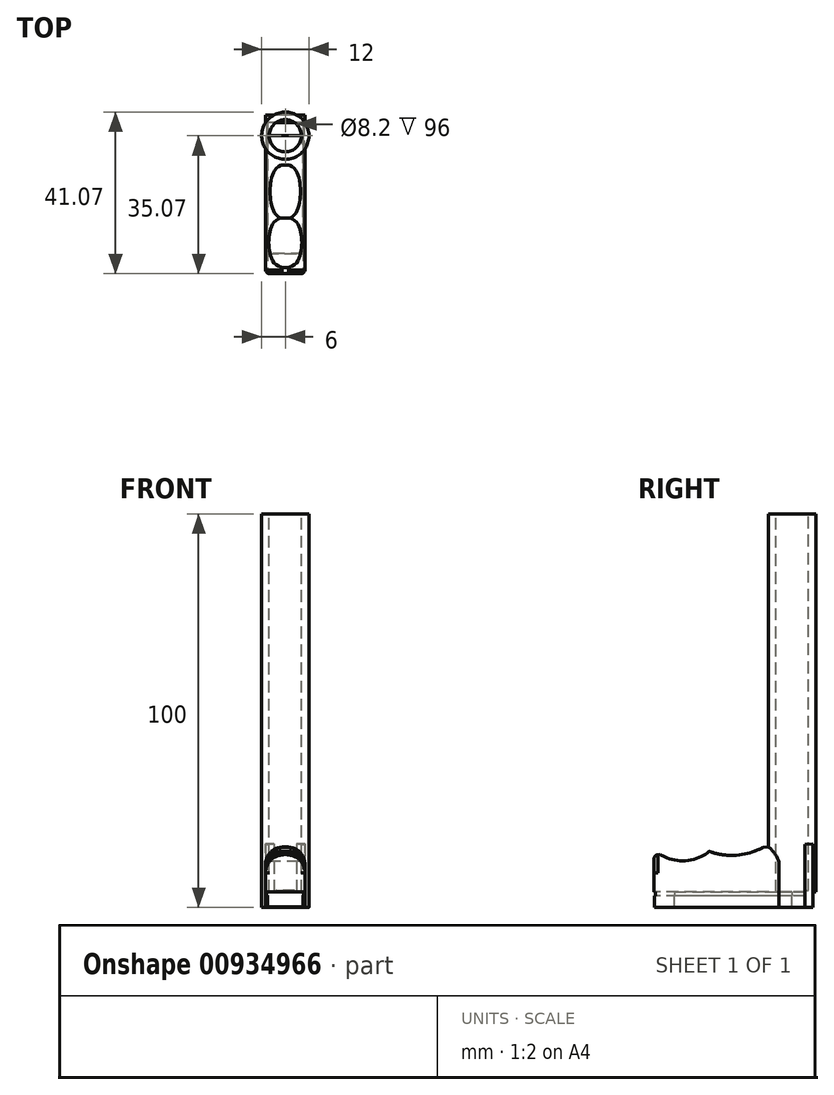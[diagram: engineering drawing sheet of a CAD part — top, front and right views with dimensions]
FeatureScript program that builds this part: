
annotation { "Feature Type Name" : "Feature", "Feature Type Description" : "" }
export const myFeature = defineFeature(function(context is Context, id is Id, definition is map)
    precondition{}
    {
        {
            var Q0;
            Q0=qCreatedBy(makeId("Top.planeOp"),FACE);
            var sketch = newSketch(context, id + "F0", { "sketchPlane" : qUnion([Q0])});
            skCircle(sketch, "E0", {"center": v(0, 0) * mm, "radius": 6 * mm});
            skSolve(sketch);
        }
        {
            var Q0;
            Q0=makeQuery(id+"F0.imprint","IMPRINT",FACE,{"disambiguationData":[TD([[makeQuery(id+"F0.imprint","IMPRINT",EDGE,{"derivedFrom":sQuery(id+"F0.wireOp",EDGE,"E0")}),1.0]])]});
            extrude(context, id + "F1", {"entities" : qUnion([Q0]), "depth" : 100 * mm, "offsetDistance" : 25 * mm});
        }
        {
            var Q0;
            Q0=qCreatedBy(makeId("Right.planeOp"),FACE);
            var sketch = newSketch(context, id + "F2", { "sketchPlane" : qUnion([Q0])});
            skLineSegment(sketch, "E1", {"start": v(-35.07, 0) * mm, "end": v(-35.07, 13.3) * mm});
            skLineSegment(sketch, "E2", {"start": v(-35.07, 0) * mm, "end": v(5.26, 0) * mm});
            skLineSegment(sketch, "E3", {"start": v(5.26, 0) * mm, "end": v(5.26, 16.15) * mm});
            skLineSegment(sketch, "E4", {"start": v(5.26, 16.15) * mm, "end": v(-35.07, 13.3) * mm});
            skSolve(sketch);
        }
        {
            var Q0;
            Q0=makeQuery(id+"F2.imprint","IMPRINT",FACE,{"disambiguationData":[TD([[makeQuery(id+"F2.imprint","IMPRINT",EDGE,{"derivedFrom":sQuery(id+"F2.wireOp",EDGE,"E1")}),-1.0]])]});
            extrude(context, id + "F3", {"entities" : qUnion([Q0]), "operationType" : NewBodyOperationType.ADD, "depth" : 5 * mm, "offsetDistance" : 25 * mm, "hasSecondDirection" : true, "secondDirectionOppositeDirection" : true, "secondDirectionDepth" : 5 * mm});
        }
        {
            var Q0;
            Q0=makeQuery(id+"F1.opExtrude","CAP_FACE",FACE,{"disambiguationData":[OSD([sQuery(id+"F0.wireOp",EDGE,"E0")])],"isStart":false});
            var sketch = newSketch(context, id + "F4", { "sketchPlane" : qUnion([Q0])});
            skCircle(sketch, "E5", {"center": v(0, 0) * mm, "radius": 4.1 * mm});
            skSolve(sketch);
        }
        {
            var Q0;
            Q0=makeQuery(id+"F4.imprint","IMPRINT",FACE,{"disambiguationData":[TD([[makeQuery(id+"F4.imprint","IMPRINT",EDGE,{"derivedFrom":sQuery(id+"F4.wireOp",EDGE,"E5")}),1.0]])]});
            extrude(context, id + "F5", {"entities" : qUnion([Q0]), "operationType" : NewBodyOperationType.REMOVE, "oppositeDirection" : true, "depth" : 125.4 * mm, "offsetDistance" : 25 * mm});
        }
        {
            var Q0;
            Q0=makeQuery(id+"F3.opExtrude","SWEPT_FACE",FACE,{"disambiguationData":[OSD([sQuery(id+"F2.wireOp",EDGE,"E1")])]});
            var sketch = newSketch(context, id + "F6", { "sketchPlane" : qUnion([Q0])});
            skLineSegment(sketch, "E6", {"start": v(-4.5, 0) * mm, "end": v(-4.5, 3) * mm});
            skLineSegment(sketch, "E7", {"start": v(-4.5, 3) * mm, "end": v(-4.74, 3) * mm});
            skLineSegment(sketch, "E8", {"start": v(-4.74, 3) * mm, "end": v(-4.74, 4) * mm});
            skLineSegment(sketch, "E9", {"start": v(-4.74, 4) * mm, "end": v(4.77, 4) * mm});
            skLineSegment(sketch, "E10", {"start": v(4.77, 4) * mm, "end": v(4.77, 3) * mm});
            skLineSegment(sketch, "E11", {"start": v(4.77, 3) * mm, "end": v(4.5, 3) * mm});
            skLineSegment(sketch, "E12", {"start": v(4.5, 3) * mm, "end": v(4.5, 0) * mm});
            skLineSegment(sketch, "E13", {"start": v(4.5, 0) * mm, "end": v(-4.5, 0) * mm});
            skSolve(sketch);
        }
        {
            var Q0;
            Q0 = qSketchRegion(id + "F6", true);
            extrude(context, id + "F7", {"entities" : qUnion([Q0]), "operationType" : NewBodyOperationType.REMOVE, "endBound" : BoundingType.THROUGH_ALL, "oppositeDirection" : true, "depth" : 25 * mm, "offsetDistance" : 25 * mm});
        }
        {
            var Q0;
            Q0=qCreatedBy(makeId("Front.planeOp"),FACE);
            var sketch = newSketch(context, id + "F8", { "sketchPlane" : qUnion([Q0])});
            skLineSegment(sketch, "E14", {"start": v(-4.45, 0.2) * mm, "end": v(-4.45, 3.1) * mm});
            skLineSegment(sketch, "E15", {"start": v(-4.45, 3.1) * mm, "end": v(-4.75, 3.1) * mm});
            skLineSegment(sketch, "E16", {"start": v(-4.75, 3.1) * mm, "end": v(-4.75, 4) * mm});
            skLineSegment(sketch, "E17", {"start": v(-4.75, 4) * mm, "end": v(4.65, 4) * mm});
            skLineSegment(sketch, "E18", {"start": v(4.65, 4) * mm, "end": v(4.65, 3.1) * mm});
            skLineSegment(sketch, "E19", {"start": v(4.65, 3.1) * mm, "end": v(4.45, 3.1) * mm});
            skLineSegment(sketch, "E20", {"start": v(4.45, 3.1) * mm, "end": v(4.45, 0.2) * mm});
            skLineSegment(sketch, "E21", {"start": v(4.45, 0.2) * mm, "end": v(-4.45, 0.2) * mm});
            skSolve(sketch);
        }
        {
            var Q0;
            Q0=makeQuery(id+"F8.imprint","IMPRINT",FACE,{"disambiguationData":[TD([[makeQuery(id+"F8.imprint","IMPRINT",EDGE,{"derivedFrom":sQuery(id+"F8.wireOp",EDGE,"E14")}),-1.0]])]});
            var Q1;
            Q1=sQuery(id+"F8.wireOp",EDGE,"E14");
            var Q2;
            Q2=sQuery(id+"F8.wireOp",EDGE,"E15");
            var Q3;
            Q3=sQuery(id+"F8.wireOp",EDGE,"E16");
            var Q4;
            Q4=sQuery(id+"F8.wireOp",EDGE,"E17");
            var Q5;
            Q5=sQuery(id+"F8.wireOp",EDGE,"E18");
            var Q6;
            Q6=sQuery(id+"F8.wireOp",EDGE,"E19");
            var Q7;
            Q7=sQuery(id+"F8.wireOp",EDGE,"E20");
            var Q8;
            Q8=sQuery(id+"F8.wireOp",EDGE,"E21");
            extrude(context, id + "F9", {"entities" : qUnion([Q0]), "surfaceEntities" : qUnion([Q1, Q2, Q3, Q4, Q5, Q6, Q7, Q8]), "depth" : 29.9 * mm, "offsetDistance" : 25 * mm});
        }
        {
            var Q0;
            {var subQ0=sQuery(id+"F2.wireOp",EDGE,"E3");var subQ1=sQuery(id+"F2.wireOp",EDGE,"E2");var subQ3=sQuery(id+"F2.wireOp",EDGE,"E4");Q0=makeQuery(id+"F3.boolean.opBoolean","SPLIT",FACE,{"disambiguationData":[TD([makeQuery(id+"F3.opExtrude","SWEPT_FACE",FACE,{"disambiguationData":[OSD([subQ0])]})])],"derivedFrom":makeQuery(id+"F3.opExtrude","CAP_FACE",FACE,{"disambiguationData":[OSD([sQuery(id+"F2.wireOp",EDGE,"E1"),subQ1,subQ0,subQ3])],"isStart":true})});}
            var sketch = newSketch(context, id + "F10", { "sketchPlane" : qUnion([Q0])});
            skLineSegment(sketch, "E22.bottom", {"start": v(-5.26, 0) * mm, "end": v(-3.32, 0) * mm});
            skLineSegment(sketch, "E22.top", {"start": v(-5.26, 4.31) * mm, "end": v(-3.32, 4.31) * mm});
            skLineSegment(sketch, "E22.left", {"start": v(-5.26, 0) * mm, "end": v(-5.26, 4.31) * mm});
            skLineSegment(sketch, "E22.right", {"start": v(-3.32, 0) * mm, "end": v(-3.32, 4.31) * mm});
            skSolve(sketch);
        }
        {
            var Q0;
            Q0=makeQuery(id+"F10.imprint","IMPRINT",FACE,{"disambiguationData":[TD([[makeQuery(id+"F10.imprint","IMPRINT",EDGE,{"derivedFrom":sQuery(id+"F10.wireOp",EDGE,"E22.bottom")}),-1.0]])]});
            extrude(context, id + "F11", {"entities" : qUnion([Q0]), "operationType" : NewBodyOperationType.ADD, "oppositeDirection" : true, "depth" : 9.9 * mm, "offsetDistance" : 25 * mm});
        }
        {
            var Q0;
            {var subQ0=sQuery(id+"F2.wireOp",EDGE,"E4");var subQ1=sQuery(id+"F2.wireOp",EDGE,"E1");Q0=makeQuery(id+"F3.boolean.opBoolean","SPLIT",EDGE,{"disambiguationData":[TD([makeQuery(id+"F3.opExtrude","SWEPT_FACE",FACE,{"disambiguationData":[OSD([subQ1])]})])],"derivedFrom":makeQuery(id+"F3.opExtrude","CAP_EDGE",EDGE,{"disambiguationData":[OSD([subQ0])],"isStart":false})});}
            var Q1;
            {var subQ0=sQuery(id+"F2.wireOp",EDGE,"E1");var subQ1=sQuery(id+"F2.wireOp",EDGE,"E4");Q1=makeQuery(id+"F3.boolean.opBoolean","SPLIT",EDGE,{"disambiguationData":[TD([makeQuery(id+"F3.opExtrude","SWEPT_FACE",FACE,{"disambiguationData":[OSD([subQ0])]})])],"derivedFrom":makeQuery(id+"F3.opExtrude","CAP_EDGE",EDGE,{"disambiguationData":[OSD([subQ1])],"isStart":true})});}
            fillet(context, id + "F12", {"entities" : qUnion([Q0, Q1]), "radius" : 4.6 * mm, "tangentPropagation" : true, "allowEdgeOverflow" : false});
        }
        {
            var Q0;
            {var subQ0=sQuery(id+"F2.wireOp",EDGE,"E1");var subQ1=makeQuery(id+"F3.opExtrude","SWEPT_FACE",FACE,{"disambiguationData":[OSD([subQ0])]});var subQ2=sQuery(id+"F2.wireOp",EDGE,"E4");Q0=makeQuery(id+"F12.opFillet","BLEND_EDGE",EDGE,{"blendedFrom":[makeQuery(id+"F3.boolean.opBoolean","SPLIT",EDGE,{"disambiguationData":[TD([subQ1])],"derivedFrom":makeQuery(id+"F3.opExtrude","CAP_EDGE",EDGE,{"disambiguationData":[OSD([subQ2])],"isStart":false})}),subQ1],"blendedInto":[subQ1]});}
            var Q1;
            {var subQ0=sQuery(id+"F2.wireOp",EDGE,"E1");var subQ1=makeQuery(id+"F3.opExtrude","SWEPT_FACE",FACE,{"disambiguationData":[OSD([subQ0])]});var subQ2=sQuery(id+"F2.wireOp",EDGE,"E4");Q1=makeQuery(id+"F12.opFillet","BLEND_EDGE",EDGE,{"blendedFrom":[makeQuery(id+"F3.boolean.opBoolean","SPLIT",EDGE,{"disambiguationData":[TD([subQ1])],"derivedFrom":makeQuery(id+"F3.opExtrude","CAP_EDGE",EDGE,{"disambiguationData":[OSD([subQ2])],"isStart":true})}),subQ1],"blendedInto":[subQ1]});}
            var Q2;
            Q2=makeQuery(id+"F3.opExtrude","SWEPT_EDGE",EDGE,{"disambiguationData":[OSD([sQuery(id+"F2.wireOp",EDGE,"E1"),sQuery(id+"F2.wireOp",EDGE,"E4")])]});
            fillet(context, id + "F13", {"entities" : qUnion([Q0, Q1, Q2]), "radius" : 1.04 * mm, "tangentPropagation" : true, "allowEdgeOverflow" : false});
        }
        {
            var Q0;
            Q0=qCreatedBy(makeId("Right.planeOp"),FACE);
            var sketch = newSketch(context, id + "F14", { "sketchPlane" : qUnion([Q0])});
            skArc(sketch, "E23", {"start": v(-33.92, 13.73) * mm, "mid": v(-27.36, 11.86) * mm, "end": v(-20.97, 14.24) * mm});
            skArc(sketch, "E24", {"start": v(-20.97, 14.24) * mm, "mid": v(-13.62, 13.3) * mm, "end": v(-6.61, 15.72) * mm});
            skLineSegment(sketch, "E25", {"start": v(-33.92, 13.73) * mm, "end": v(-6.61, 15.72) * mm});
            skSolve(sketch);
        }
        {
            var Q0;
            Q0 = qSketchRegion(id + "F14", true);
            extrude(context, id + "F15", {"entities" : qUnion([Q0]), "operationType" : NewBodyOperationType.REMOVE, "oppositeDirection" : true, "depth" : 25 * mm, "offsetDistance" : 25 * mm, "hasSecondDirection" : true, "secondDirectionOppositeDirection" : false, "secondDirectionDepth" : 25 * mm});
        }
    });
